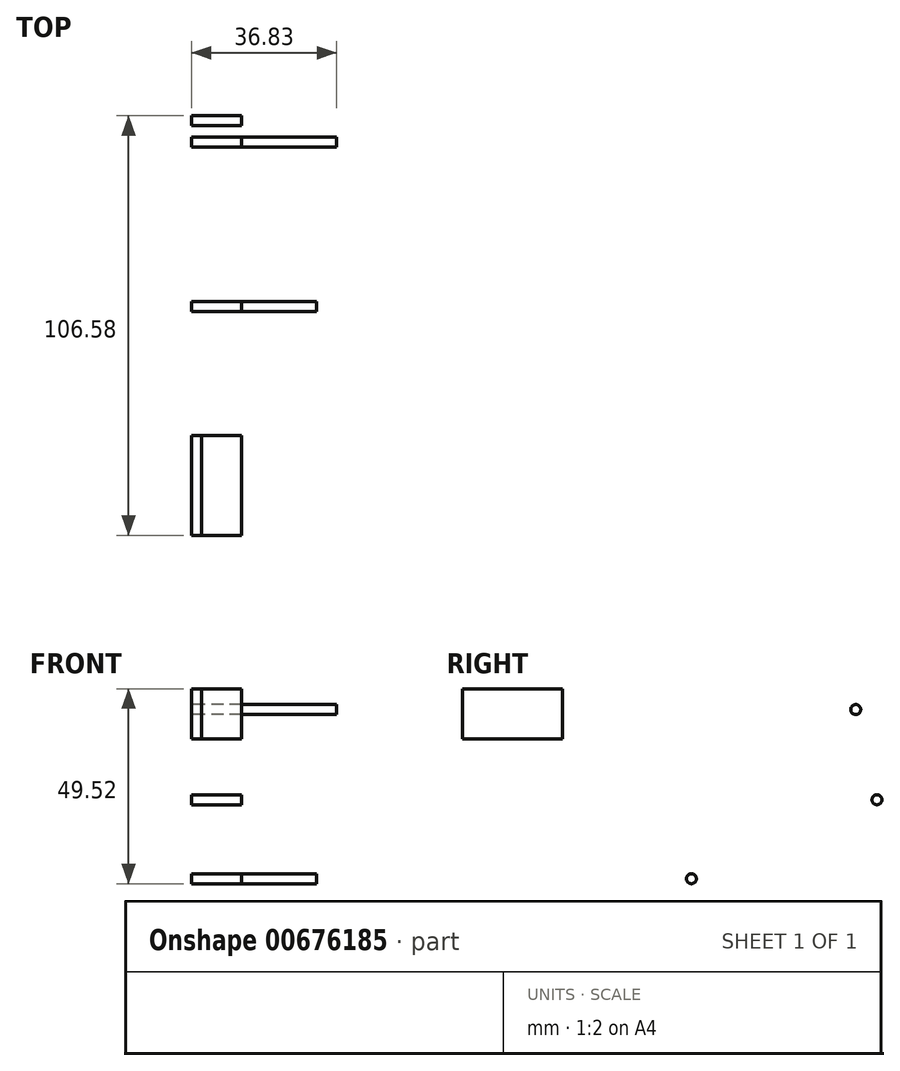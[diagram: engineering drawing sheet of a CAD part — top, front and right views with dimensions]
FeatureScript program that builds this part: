
annotation { "Feature Type Name" : "Feature", "Feature Type Description" : "" }
export const myFeature = defineFeature(function(context is Context, id is Id, definition is map)
    precondition{}
    {
        {
            var Q0;
            Q0=qCreatedBy(makeId("Right.planeOp"),FACE);
            var sketch = newSketch(context, id + "F0", { "sketchPlane" : qUnion([Q0])});
            skCircle(sketch, "E0", {"center": v(0, 0) * mm, "radius": 1.27 * mm});
            skCircle(sketch, "E1", {"center": v(41.76, 42.97) * mm, "radius": 1.27 * mm});
            skLineSegment(sketch, "E2.bottom", {"start": v(-32.77, 48.25) * mm, "end": v(-58.17, 48.25) * mm});
            skLineSegment(sketch, "E2.top", {"start": v(-32.77, 35.55) * mm, "end": v(-58.17, 35.55) * mm});
            skLineSegment(sketch, "E2.left", {"start": v(-32.77, 48.25) * mm, "end": v(-32.77, 35.55) * mm});
            skLineSegment(sketch, "E2.right", {"start": v(-58.17, 48.25) * mm, "end": v(-58.17, 35.55) * mm});
            skCircle(sketch, "E3", {"center": v(47.14, 20.07) * mm, "radius": 1.27 * mm});
            skSolve(sketch);
        }
        {
            var Q0;
            Q0=makeQuery(id+"F0.imprint","IMPRINT",FACE,{"disambiguationData":[TD([[makeQuery(id+"F0.imprint","IMPRINT",EDGE,{"derivedFrom":sQuery(id+"F0.wireOp",EDGE,"E0")}),1.0]])]});
            extrude(context, id + "F1", {"entities" : qUnion([Q0]), "depth" : 31.75 * mm, "offsetDistance" : 25.4 * mm});
        }
        {
            var Q0;
            Q0=makeQuery(id+"F0.imprint","IMPRINT",FACE,{"disambiguationData":[TD([[makeQuery(id+"F0.imprint","IMPRINT",EDGE,{"derivedFrom":sQuery(id+"F0.wireOp",EDGE,"E1")}),1.0]])]});
            extrude(context, id + "F2", {"entities" : qUnion([Q0]), "depth" : 36.83 * mm, "offsetDistance" : 25.4 * mm});
        }
        {
            var Q0;
            Q0=makeQuery(id+"F0.imprint","IMPRINT",FACE,{"disambiguationData":[TD([[makeQuery(id+"F0.imprint","IMPRINT",EDGE,{"derivedFrom":sQuery(id+"F0.wireOp",EDGE,"E2.bottom")}),1.0]])]});
            extrude(context, id + "F3", {"entities" : qUnion([Q0]), "depth" : 2.54 * mm, "offsetDistance" : 25.4 * mm});
        }
        {
            var Q0;
            Q0 = qSketchRegion(id + "F0", true);
            extrude(context, id + "F4", {"entities" : qUnion([Q0]), "depth" : 12.7 * mm, "offsetDistance" : 25.4 * mm});
        }
    });
